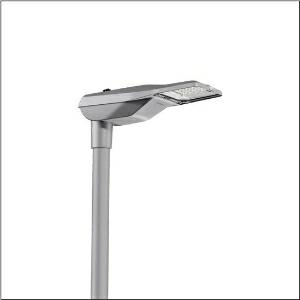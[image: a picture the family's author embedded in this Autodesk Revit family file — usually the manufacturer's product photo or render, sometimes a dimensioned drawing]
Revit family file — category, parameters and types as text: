
# Revit family: streetlight_sl_21_micro___p0_5a_5xe1v33s08db_1111
name_source: partatom
category: Lighting Fixtures
units: mm (PartAtom-declared; Revit-internal decimal feet)

## family parameters
Cut with Voids When Loaded = No
Host = Face
Light Source = No
Part Type = Normal
Room Calculation Point = No
Round Connector Dimension = Use Diameter
Shared = No

## types (1)
- --- (1 x LED, 4940 lm, 39.1 W, 3000K)
    Apparent Load = 39 VA
    CIE Flux Codes = 37 73 96 100 100
    Color Rendering = 70
    Color Temperature = 3000K
    Default Elevation = 1800 mm
    Description = Streetlight SL 21 micro, mast luminaire, primary light control with lens, of PMMA, primary optical cover: cover, of toughened safety glass, transparent, light distribution: P0.5a, light emission: direct distribution, primary light characteristic: asymmetric, installation type: post-top, side-entry, LED, High Power LED, rated luminous flux: 4.940lm, luminous efficacy: 126lm/W, light colour: 730, colour temperature: 3000K, control gear: D4i, control: pre-setting: logarithmic dimming characteristic, flexible luminous flux parameterisation, time-dependent luminous flux control, constant luminous flux control, overheat protection, mains connection: 220..240V, AC, 50/60Hz, start of lifetime: 39W, end of service life: 41W, reduction: 18W, luminaire housing, of diecast aluminium, powder-coated, Siteco® metallic grey (DB 702S), corrosivity category C5 mid according to DIN EN ISO 12944, multi-level sealing system, sealing non-destructively replaceable, inclination adjustable: 0°, 5°, 10°, 15°, please order mast flange separately, length: 528mm, width: 235mm, height: 110mm, mast flange for spigot size: 42mm (side-entry): 5XC10008XM4, 60/48mm (side-entry/post-top): 5XC10108XM2, 76/60mm (side-entry/post-top): 5XC10108XM1, Smart Interface above, protection rating (complete): IP66, insulation class (complete): insulation class II (safety insulation), certification: CE, ENEC, ENEC+, VDE, impact resistance: IK10, permissible operating ambient temperature for outdoor applications: -40..+50°C, standard-compliant lighting for roads and squares, packaging unit: 1 piece

Light Distribution: P0.5a
    Height = 110 mm
    Lamp = 1 x LED
    Lamp Light Flux = 4940 lm
    Lamp Power = 39.1 W
    Lamp count = 1
    Length = 528 mm
    Luminous efficacy = 126 lm/W
    Manufacturer = Siteco
    ModVariant = No
    Model = 5XE1V33S08DB
    Number of Poles = 1
    OnlyDefault = Yes
    Power Factor = 1
    Product Name = Streetlight SL 21 micro | P0.5a
    Product group = mast luminaire | pylon top
    ProductGroupID = 6100
    Protection Class = Protection class II
    Protection Degree = IP 66
    RLX_Detail_Level = 1
    RLX_Emergency_Light_Flux = 0 lm
    RLX_Emergency_Type = 0
    RLX_Emergency_Type_DB = No
    RlxData = <blob elided: 98373 chars, md5=c714889d>
    Socket = socket
    Standby Power = 0 W
    System Light Flux = 4940 lm
    System Power = 39 W
    Type Comments = factory setting: luminous flux: 100 % | dim-lin: 254 | 765 mA
    Type Image = l_1277292.jpg
    URL = http://relux.com
    VarID = @adj_070104
    Voltage = 0 V
    Weight = 0.00 kg
    Width = 235 mm

## geometry (parser evidence)
native form markers: Blend x4, Sweep x10
no freeform markers — native parametric forms only
